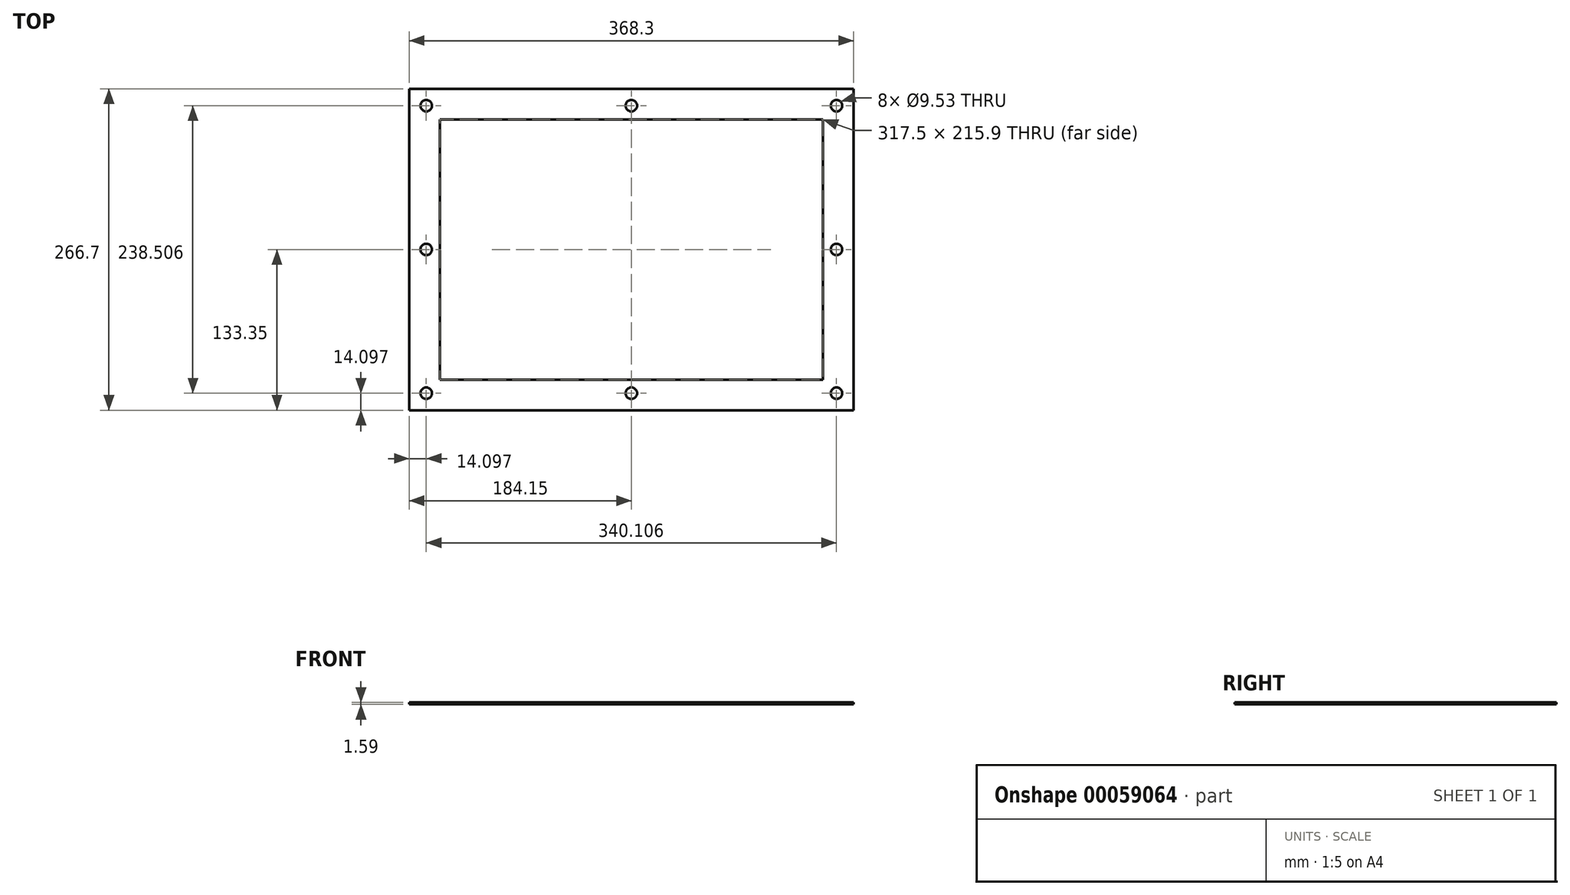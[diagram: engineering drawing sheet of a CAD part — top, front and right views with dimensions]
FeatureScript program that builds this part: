
annotation { "Feature Type Name" : "Feature", "Feature Type Description" : "" }
export const myFeature = defineFeature(function(context is Context, id is Id, definition is map)
    precondition{}
    {
        {
            var Q0;
            Q0=qCreatedBy(makeId("Top.planeOp"),FACE);
            var sketch = newSketch(context, id + "F0", { "sketchPlane" : qUnion([Q0])});
            skLineSegment(sketch, "E0.bottom", {"start": v(184.15, -133.35) * mm, "end": v(-184.15, -133.35) * mm});
            skLineSegment(sketch, "E0.top", {"start": v(184.15, 133.35) * mm, "end": v(-184.15, 133.35) * mm});
            skLineSegment(sketch, "E0.left", {"start": v(184.15, -133.35) * mm, "end": v(184.15, 133.35) * mm});
            skLineSegment(sketch, "E0.right", {"start": v(-184.15, -133.35) * mm, "end": v(-184.15, 133.35) * mm});
            skPoint(sketch, "E0.middle", {"position": v(0, 0) * mm});
            skLineSegment(sketch, "E1.0", {"start": v(158.75, 107.95) * mm, "end": v(-158.75, 107.95) * mm});
            skLineSegment(sketch, "E1.1", {"start": v(158.75, -107.95) * mm, "end": v(158.75, 107.95) * mm});
            skLineSegment(sketch, "E1.2", {"start": v(158.75, -107.95) * mm, "end": v(-158.75, -107.95) * mm});
            skLineSegment(sketch, "E1.3", {"start": v(-158.75, -107.95) * mm, "end": v(-158.75, 107.95) * mm});
            skCircle(sketch, "E2", {"center": v(170.05, 0) * mm, "radius": 3.18 * mm, "construction": true});
            skPoint(sketch, "E2.centerSnap0", {"position": v(184.15, 0) * mm});
            skLineSegment(sketch, "E3.0", {"start": v(-170.05, -119.25) * mm, "end": v(-170.05, 119.25) * mm, "construction": true});
            skLineSegment(sketch, "E3.1", {"start": v(170.05, -119.25) * mm, "end": v(-170.05, -119.25) * mm, "construction": true});
            skLineSegment(sketch, "E3.2", {"start": v(170.05, -119.25) * mm, "end": v(170.05, 119.25) * mm, "construction": true});
            skLineSegment(sketch, "E3.3", {"start": v(170.05, 119.25) * mm, "end": v(-170.05, 119.25) * mm, "construction": true});
            skCircle(sketch, "E4", {"center": v(170.05, 119.25) * mm, "radius": 3.18 * mm, "construction": true});
            skCircle(sketch, "E5", {"center": v(0, 119.25) * mm, "radius": 3.18 * mm, "construction": true});
            skCircle(sketch, "E6", {"center": v(-170.05, 119.25) * mm, "radius": 3.18 * mm, "construction": true});
            skCircle(sketch, "E7.1.0", {"center": v(170.05, -119.25) * mm, "radius": 3.18 * mm, "construction": true});
            skCircle(sketch, "E7.1.1", {"center": v(-170.05, -119.25) * mm, "radius": 3.18 * mm, "construction": true});
            skCircle(sketch, "E7.1.2", {"center": v(0, -119.25) * mm, "radius": 3.18 * mm, "construction": true});
            skCircle(sketch, "E7.1.3", {"center": v(-170.05, 0) * mm, "radius": 3.18 * mm, "construction": true});
            skCircle(sketch, "E8", {"center": v(-170.05, 119.25) * mm, "radius": 4.76 * mm});
            skCircle(sketch, "E9", {"center": v(0, 119.25) * mm, "radius": 4.76 * mm});
            skCircle(sketch, "E10", {"center": v(170.05, 119.25) * mm, "radius": 4.76 * mm});
            skCircle(sketch, "E11", {"center": v(170.05, 0) * mm, "radius": 4.76 * mm});
            skCircle(sketch, "E12.1.0", {"center": v(0, -119.25) * mm, "radius": 4.76 * mm});
            skCircle(sketch, "E12.1.1", {"center": v(-170.05, -119.25) * mm, "radius": 4.76 * mm});
            skCircle(sketch, "E12.1.2", {"center": v(170.05, -119.25) * mm, "radius": 4.76 * mm});
            skCircle(sketch, "E12.1.3", {"center": v(-170.05, 0) * mm, "radius": 4.76 * mm});
            skSolve(sketch);
        }
        {
            var Q0;
            Q0=makeQuery(id+"F0.imprint","IMPRINT",FACE,{"disambiguationData":[TD([[makeQuery(id+"F0.imprint","IMPRINT",EDGE,{"derivedFrom":sQuery(id+"F0.wireOp",EDGE,"E0.bottom")}),-1.0]])]});
            extrude(context, id + "F1", {"entities" : qUnion([Q0]), "depth" : 1.59 * mm});
        }
    });
